# Revit family: Shower_System_Valve-Symmons-Dia-Shower-Volume_Control-Trim
name_source: partatom
category: Plumbing Fixtures
revit_build: Autodesk Revit 2015 (Build: 20140606_1530(x64)
units: mm (PartAtom-declared; Revit-internal decimal feet)

## types (4) — shared parameters
Date Modified = January 30, 2015
Default Elevation = 32 "
Equipment Abbreviation = SVS
Family Version = 1.0
Manufacturer = Symmons Industries, Inc.
Model Disclaimer = Contact Symmons Industries, Inc. For More Information
Product Documentation Link = http://www.symmons.com
Product Page URL = http://www.symmons.com
Product data url = https://bimobject.com
URL = http://www.symmons.com
z Error = No
z Error Type = 1
z Has .5 Inch Female IPS Connections = No
z Has Check Stops = No
z Has Integral Service Stops = No
z Has Reverse Core = No
z Has Symmons Temptrol Mixing Valve Only = No
z Has Volume Control = Yes
z Has Wide Lever Handle = No
z Mixer Valve Visibility = No
z Modification Selection = Volume Control
z Trim Visibility = Yes
z VC Type = 1
z VC Visibility = Yes
zero-valued in all types: z Type Check Stops, z Type IPS Connection, z Type Reverse Core, z Type Service Stop, z Type Wide Lever

## per-type parameters (varying)
| type | Description | Model | Product Material | z Has Rebuild Kit Trim Only | z Has Trim Only | z Option Selection | z Type All | z Type Finish | z Type Kit | z Type Model | z Type Trim |
| Trim, Chrome | Trim only, mixing valve ordered separately, Chrome | S-3500-CYL-B-TRM | Chrome - Symmons - Polished | No | Yes | Trim Only | 6000001 | 1 | 0 | 6 | 1 |
| Trim, Satin Nickel | Trim only, mixing valve ordered separately, Satin Nickel | S-3500-CYL-B-STN-TRM | Nickel - Symmons - Satin | No | Yes | Trim Only | 6000002 | 2 | 0 | 6 | 1 |
| Rebuild Kit, Chrome | Rebuild kit, Trim only, Chrome | S-3500-CYL-B-REB-TRM | Chrome - Symmons - Polished | Yes | No | Rebuild Kit Trim Only | 7000001 | 1 | 1 | 7 | 0 |
| Rebuild Kit, Satin Nickel | Rebuild kit, Trim only, Satin Nickel | S-3500-CYL-B-STN-REB-TRM | Nickel - Symmons - Satin | Yes | No | Rebuild Kit Trim Only | 7000002 | 2 | 1 | 7 | 0 |

## geometry (parser evidence)
native form markers: Blend x4, Sweep x3
no freeform markers — native parametric forms only
